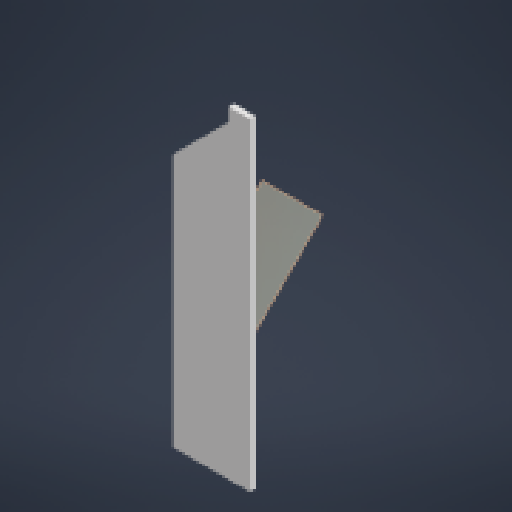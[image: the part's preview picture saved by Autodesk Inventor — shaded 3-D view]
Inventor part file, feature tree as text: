
AUTODESK INVENTOR PART (.ipt)
format: ipt  version: 2023 (Build 270158000, 158)  size: 164,352 bytes
history: native  units: in
note: dims shown in document units (in); Inventor stores cm internally (conversion verified against a paired STEP export)
features: reference x18, other x6, sketch x3, extrude x2, plane x1, hole x1
ambient origin geometry x8: Origin, YZ Plane, XZ Plane, XY Plane, X Axis, Y Axis, Z Axis, Center Point
bodies: Solid1 (feature_tree)
feature tree (31):
  extrude  "Extrusion1"  Depth=0.0394in
  plane  "Work Plane2"
  extrude  "Extrusion2"  Depth=0.1181in
  hole  "Hole1"  [1 undecoded]
  sketch  "Sketch1"  dims[d2=0.0118in d3=0.0394in]
  reference  "Reference1"
  reference  "Reference2"
  reference  "Reference4"
  reference  "Reference5"
  reference  "Reference6"
  reference  "Reference7"
  reference  "Reference8"
  reference  "Reference9"
  reference  "Reference10"
  reference  "Reference11"
  sketch  "Sketch3"  dims[d4=0.1181in d5=0.0in d6=0.0591in]
  reference  "Reference12"
  reference  "Reference13"
  reference  "Reference14"
  reference  "Reference15"
  sketch  "Sketch4"  dims[d7=0.0591in d8=0.0591in d9=0.0591in d10=0.0in d11=0.0in d12=0.1339in d13=0.2362in d14=0.248in d15=0.0787in d16=90.0deg d17=0.315in d18=0.8108in d19=1.1811in]
  reference  "Reference16"
  reference  "Reference17"
  reference  "Reference18"
  reference  "Reference19"
  other  "Assembly2"
  other  "blacha:1"
  other  "mocowanie-czujnika-pr:1"
  other  "PLUG:1"
  other  "sds02a-with-sensor:2"
  other  "mocowanie-czujnika-p:1"
note: 1 required parameter value undecoded (feature->parameter linkage not recoverable at this tier; creation-order binding heuristic only, values carry confidence <= 0.55)
